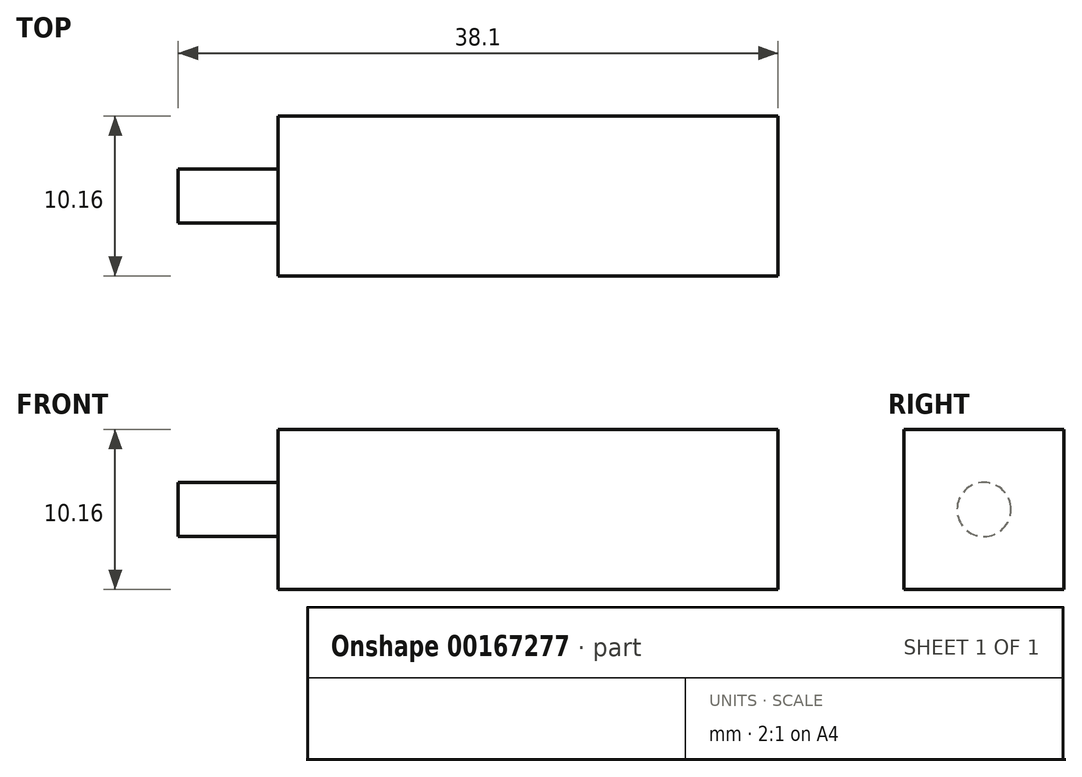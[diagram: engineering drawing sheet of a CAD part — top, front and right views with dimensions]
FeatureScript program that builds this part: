
annotation { "Feature Type Name" : "Feature", "Feature Type Description" : "" }
export const myFeature = defineFeature(function(context is Context, id is Id, definition is map)
    precondition{}
    {
        {
            var Q0;
            Q0=qCreatedBy(makeId("Right.planeOp"),FACE);
            var sketch = newSketch(context, id + "F0", { "sketchPlane" : qUnion([Q0])});
            skLineSegment(sketch, "E0.bottom", {"start": v(0, 0) * mm, "end": v(-10.16, 0) * mm});
            skLineSegment(sketch, "E0.top", {"start": v(0, 10.16) * mm, "end": v(-10.16, 10.16) * mm});
            skLineSegment(sketch, "E0.left", {"start": v(0, 0) * mm, "end": v(0, 10.16) * mm});
            skLineSegment(sketch, "E0.right", {"start": v(-10.16, 0) * mm, "end": v(-10.16, 10.16) * mm});
            skSolve(sketch);
        }
        {
            var Q0;
            Q0=makeQuery(id+"F0.imprint","IMPRINT",FACE,{"disambiguationData":[TD([[makeQuery(id+"F0.imprint","IMPRINT",EDGE,{"derivedFrom":sQuery(id+"F0.wireOp",EDGE,"E0.bottom")}),-1.0]])]});
            extrude(context, id + "F1", {"entities" : qUnion([Q0]), "depth" : 31.75 * mm});
        }
        {
            var Q0;
            Q0=qCreatedBy(makeId("Right.planeOp"),FACE);
            var sketch = newSketch(context, id + "F2", { "sketchPlane" : qUnion([Q0])});
            skCircle(sketch, "E1", {"center": v(-5.08, 5.08) * mm, "radius": 1.71 * mm});
            skPoint(sketch, "E1.centerSnap0", {"position": v(-5.08, 10.16) * mm});
            skPoint(sketch, "E1.centerSnap1", {"position": v(-10.16, 5.08) * mm});
            skSolve(sketch);
        }
        {
            var Q0;
            Q0 = qSketchRegion(id + "F2", true);
            extrude(context, id + "F3", {"entities" : qUnion([Q0]), "operationType" : NewBodyOperationType.ADD, "oppositeDirection" : true, "depth" : 6.35 * mm});
        }
    });
